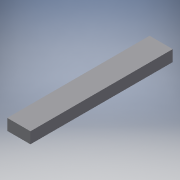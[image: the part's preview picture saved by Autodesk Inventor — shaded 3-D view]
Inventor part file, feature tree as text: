
AUTODESK INVENTOR PART (.ipt)
format: ipt  version: 2017 (Build 210142000, 142)  size: 90,624 bytes
history: native  units: in
note: dims shown in document units (in); Inventor stores cm internally (conversion verified against a paired STEP export)
features: extrude x1, sketch x1
ambient origin geometry x8: Origin, YZ Plane, XZ Plane, XY Plane, X Axis, Y Axis, Z Axis, Center Point
bodies: Solid1 (feature_tree)
feature tree (2):
  extrude  "Extrusion1"  Depth=9.5in
  sketch  "Sketch1"  dims[d0=1.547in d1=9.5in d2=0.75in d3=0.0in]
